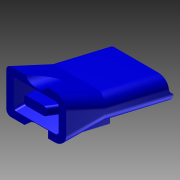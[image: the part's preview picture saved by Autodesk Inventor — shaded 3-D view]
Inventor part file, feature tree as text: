
AUTODESK INVENTOR PART (.ipt)
format: ipt  version: 2012 (Build 160160000, 160)  size: 288,768 bytes
history: native  units: mm
features: extrude x10, sketch x10, fillet x5, chamfer x1, plane x1
ambient origin geometry x8: Origin, YZ Plane, XZ Plane, XY Plane, X Axis, Y Axis, Z Axis, Center Point
bodies: Solid1 (feature_tree)
feature tree (27):
  extrude  "Extrusion1"  Depth=30.0mm
  extrude  "Extrusion2"  Depth=24.0mm
  extrude  "Extrusion3"  Depth=3.0mm
  extrude  "Extrusion4"  Depth=17.5mm TaperAngle=0.0deg
  fillet  "Fillet1"  Radius=9.5mm
  fillet  "Fillet2"  Radius=13.5mm
  fillet  "Fillet3"  Radius=3.0mm
  extrude  "Extrusion5"  Depth=3.0mm TaperAngle=0.0deg
  chamfer  "Chamfer1"  Distance=3.0mm
  extrude  "Extrusion6"  Depth=3.0mm TaperAngle=0.0deg
  fillet  "Fillet4"  Radius=3.0mm
  extrude  "Extrusion7"  Depth=2.0mm
  extrude  "Extrusion8"  Depth=13.0mm
  plane  "Work Plane1"
  extrude  "Extrusion11"  Depth=13.5mm TaperAngle=0.0deg
  fillet  "Fillet5"  Radius=13.5mm
  extrude  "Extrusion13"  Depth=17.5mm
  sketch  "Sketch1"  dims[d0=19.5mm d1=30.0mm]
  sketch  "Sketch2"  dims[d2=24.0mm d3=24.0mm]
  sketch  "Sketch5"  dims[d12=3.0mm d13=3.0mm d14=24.0mm d15=0.0mm d16=0.0mm]
  sketch  "Sketch6"  dims[d17=9.5mm d18=13.5mm d19=3.0mm d20=3.0mm]
  sketch  "Sketch7"  dims[d21=3.5mm]
  sketch  "Sketch8"  dims[d22=1.5mm d23=3.0mm d24=0.0mm]
  sketch  "Sketch11"  dims[d25=19.5mm d26=30.0mm d27=24.0mm d28=24.0mm d29=13.5mm d30=3.0mm d31=3.0mm d32=3.0mm d33=0.0mm d34=3.0mm]
  sketch  "Sketch13"  dims[d35=4.0mm d36=2.0mm d37=13.0mm d38=13.5mm d39=0.0mm d40=13.5mm d41=4.0mm d42=45.0deg d43=17.5mm d44=3.5mm d45=0.0mm d46=1.0mm d47=3.0mm d49=2.5mm d50=4.0mm d51=0.0mm d52=2.0mm d53=0.0mm d61=5.0mm d62=10.0mm d63=10.0mm d64=0.0mm d65=0.5mm d68=16.0mm d70=4.5mm d71=5.0mm d72=18.0mm d73=10.0mm d74=0.0mm]
  sketch  "Sketch3"  dims[d4=13.5mm d5=3.0mm]
  sketch  "Sketch4"  dims[d6=3.0mm d7=17.5mm d8=0.0mm d9=9.5mm d10=13.5mm d11=3.0mm]
